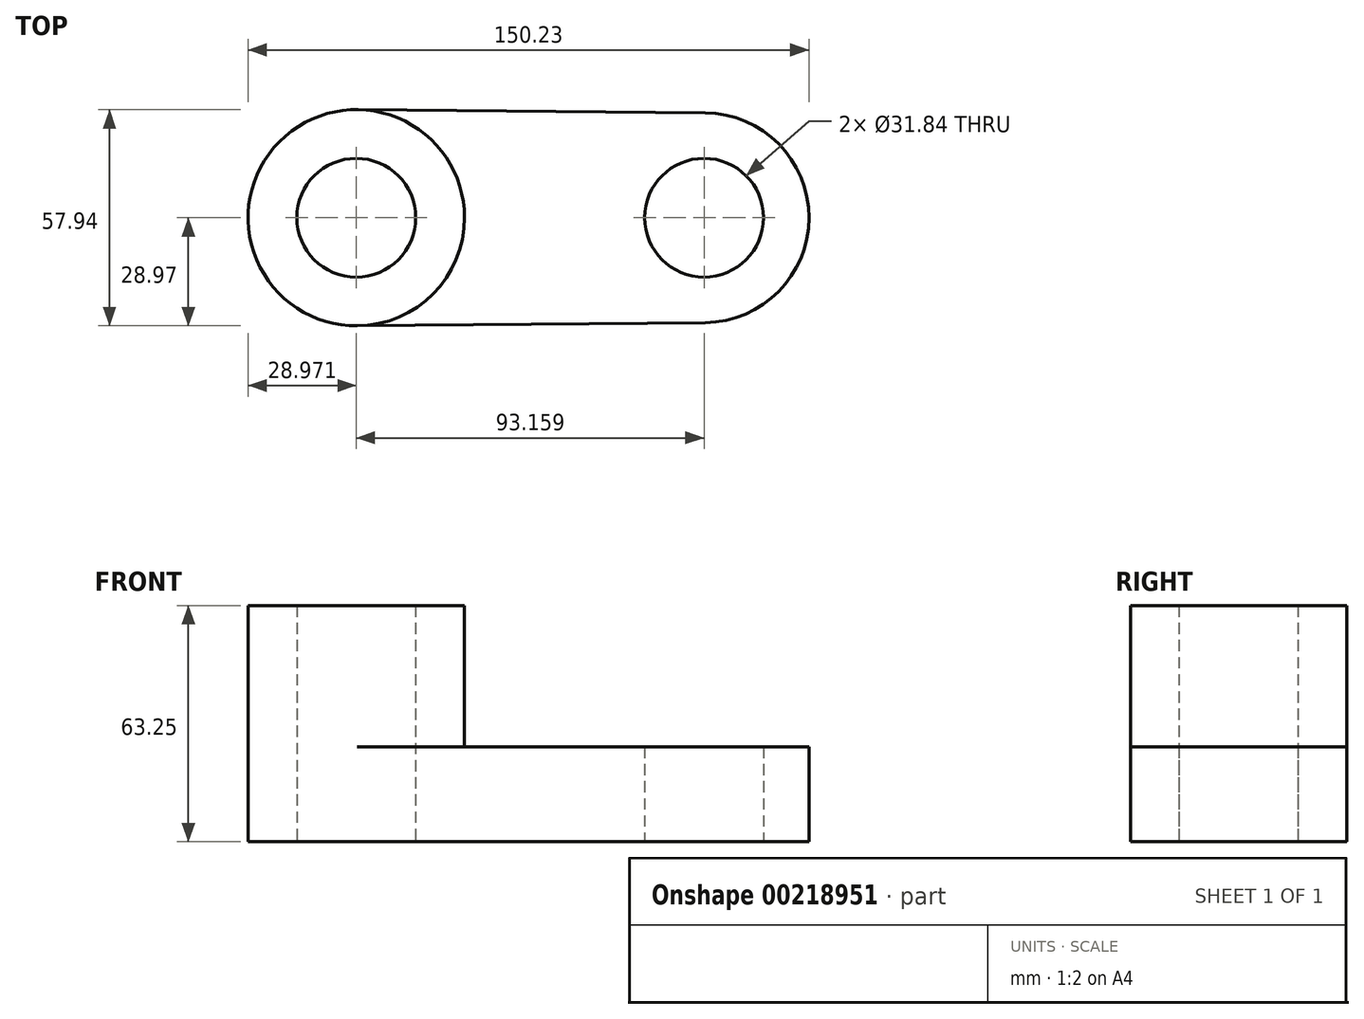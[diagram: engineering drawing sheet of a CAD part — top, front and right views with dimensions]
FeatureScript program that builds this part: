
annotation { "Feature Type Name" : "Feature", "Feature Type Description" : "" }
export const myFeature = defineFeature(function(context is Context, id is Id, definition is map)
    precondition{}
    {
        {
            var Q0;
            Q0=qCreatedBy(makeId("Top.planeOp"),FACE);
            var sketch = newSketch(context, id + "F0", { "sketchPlane" : qUnion([Q0])});
            skCircle(sketch, "E0", {"center": v(-46.58, 0) * mm, "radius": 15.92 * mm});
            skCircle(sketch, "E1", {"center": v(46.58, 0) * mm, "radius": 15.92 * mm});
            skArc(sketch, "E2", {"start": v(-46.3, 28.97) * mm, "mid": v(-75.55, 0) * mm, "end": v(-46.3, -28.97) * mm});
            skArc(sketch, "E3", {"start": v(46.84, -28.1) * mm, "mid": v(74.68, 0) * mm, "end": v(46.84, 28.1) * mm});
            skLineSegment(sketch, "E4", {"start": v(-46.3, 28.97) * mm, "end": v(46.84, 28.1) * mm});
            skLineSegment(sketch, "E5", {"start": v(46.84, -28.1) * mm, "end": v(-46.3, -28.97) * mm});
            skArc(sketch, "E6", {"start": v(-46.3, -28.97) * mm, "mid": v(-17.6, 0) * mm, "end": v(-46.3, 28.97) * mm});
            skSolve(sketch);
        }
        {
            var Q0;
            Q0=makeQuery(id+"F0.imprint","IMPRINT",FACE,{"disambiguationData":[TD([[makeQuery(id+"F0.imprint","IMPRINT",EDGE,{"derivedFrom":sQuery(id+"F0.wireOp",EDGE,"E1")}),-1.0]])]});
            extrude(context, id + "F1", {"entities" : qUnion([Q0]), "depth" : 25.4 * mm});
        }
        {
            var Q0;
            Q0=makeQuery(id+"F0.imprint","IMPRINT",FACE,{"disambiguationData":[TD([[makeQuery(id+"F0.imprint","IMPRINT",EDGE,{"derivedFrom":sQuery(id+"F0.wireOp",EDGE,"E0")}),-1.0]])]});
            extrude(context, id + "F2", {"entities" : qUnion([Q0]), "operationType" : NewBodyOperationType.ADD, "depth" : 63.25 * mm});
        }
    });
